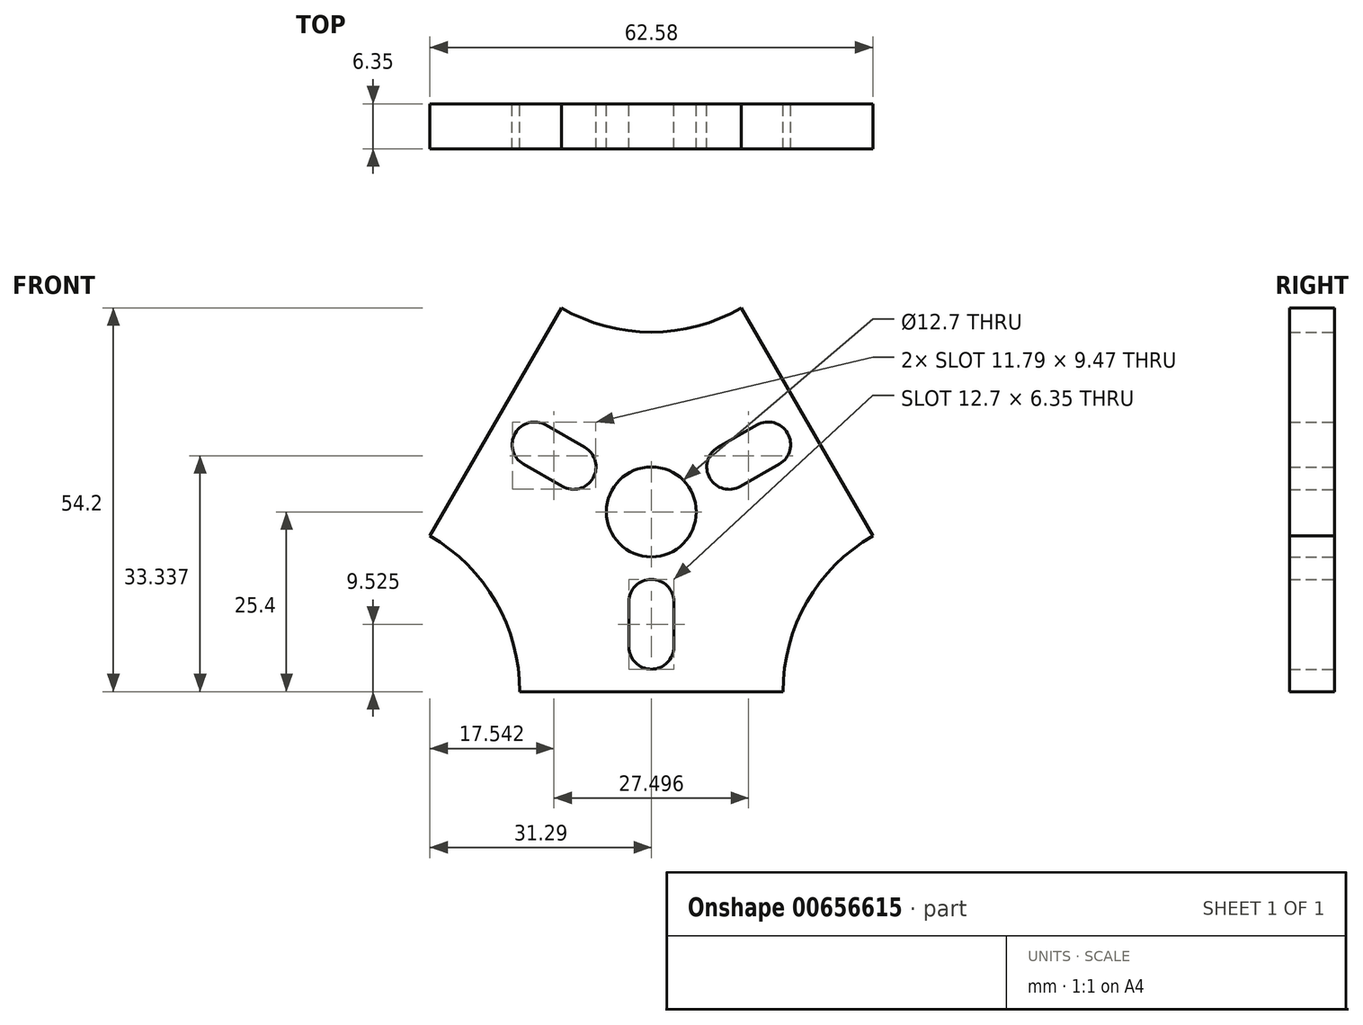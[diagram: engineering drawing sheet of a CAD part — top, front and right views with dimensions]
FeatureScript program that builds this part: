
annotation { "Feature Type Name" : "Feature", "Feature Type Description" : "" }
export const myFeature = defineFeature(function(context is Context, id is Id, definition is map)
    precondition{}
    {
        {
            var Q0;
            Q0=qCreatedBy(makeId("Front.planeOp"),FACE);
            var sketch = newSketch(context, id + "F0", { "sketchPlane" : qUnion([Q0])});
            skCircle(sketch, "E0", {"center": v(0, 0) * mm, "radius": 6.35 * mm});
            skCircle(sketch, "E1.cCircle", {"center": v(0, 0) * mm, "radius": 25.4 * mm, "construction": true});
            skLineSegment(sketch, "E1.0", {"start": v(44, -25.4) * mm, "end": v(-44, -25.4) * mm});
            skLineSegment(sketch, "E1.1", {"start": v(-44, -25.4) * mm, "end": v(0, 50.8) * mm});
            skLineSegment(sketch, "E1.2", {"start": v(0, 50.8) * mm, "end": v(44, -25.4) * mm});
            skPoint(sketch, "E1.0.midPoint", {"position": v(0, -25.4) * mm});
            skCircle(sketch, "E2", {"center": v(0, 0) * mm, "radius": 38.1 * mm});
            skCircle(sketch, "E3", {"center": v(-44, -25.4) * mm, "radius": 25.4 * mm});
            skCircle(sketch, "E4", {"center": v(0, 50.8) * mm, "radius": 25.4 * mm});
            skCircle(sketch, "E5", {"center": v(44, -25.4) * mm, "radius": 25.4 * mm});
            skSolve(sketch);
        }
        {
            var Q0;
            Q0=makeQuery(id+"F0.imprint","IMPRINT",FACE,{"disambiguationData":[TD([[makeQuery(id+"F0.imprint","IMPRINT",EDGE,{"derivedFrom":sQuery(id+"F0.wireOp",EDGE,"E0")}),-1.0]])]});
            extrude(context, id + "F1", {"entities" : qUnion([Q0]), "depth" : 6.35 * mm, "offsetDistance" : 25.4 * mm});
        }
        {
            var Q0;
            Q0=qCreatedBy(makeId("Front.planeOp"),FACE);
            var sketch = newSketch(context, id + "F2", { "sketchPlane" : qUnion([Q0])});
            skPoint(sketch, "E6.center", {"position": v(0, 0) * mm});
            skArc(sketch, "E7", {"start": v(-3.17, -19.05) * mm, "mid": v(0, -22.23) * mm, "end": v(3.17, -19.05) * mm});
            skArc(sketch, "E8", {"start": v(3.18, -12.7) * mm, "mid": v(0, -9.53) * mm, "end": v(-3.18, -12.7) * mm});
            skLineSegment(sketch, "E9", {"start": v(-3.18, -12.7) * mm, "end": v(-3.17, -19.05) * mm});
            skLineSegment(sketch, "E10", {"start": v(3.17, -19.05) * mm, "end": v(3.17, -12.7) * mm});
            skArc(sketch, "E11.1.0", {"start": v(12.59, -3.6) * mm, "mid": v(8.25, -4.76) * mm, "end": v(9.41, -9.1) * mm});
            skLineSegment(sketch, "E11.1.1", {"start": v(18.09, -6.78) * mm, "end": v(12.59, -3.6) * mm});
            skArc(sketch, "E11.1.2", {"start": v(14.91, -12.27) * mm, "mid": v(19.25, -11.11) * mm, "end": v(18.09, -6.78) * mm});
            skLineSegment(sketch, "E11.1.3", {"start": v(9.41, -9.1) * mm, "end": v(14.91, -12.27) * mm});
            skArc(sketch, "E11.2.0", {"start": v(9.41, 9.1) * mm, "mid": v(8.25, 4.76) * mm, "end": v(12.59, 3.6) * mm});
            skLineSegment(sketch, "E11.2.1", {"start": v(14.91, 12.27) * mm, "end": v(9.41, 9.1) * mm});
            skArc(sketch, "E11.2.2", {"start": v(18.09, 6.78) * mm, "mid": v(19.25, 11.11) * mm, "end": v(14.91, 12.27) * mm});
            skLineSegment(sketch, "E11.2.3", {"start": v(12.59, 3.6) * mm, "end": v(18.09, 6.78) * mm});
            skArc(sketch, "E11.3.0", {"start": v(-3.17, 12.7) * mm, "mid": v(0, 9.53) * mm, "end": v(3.18, 12.7) * mm});
            skLineSegment(sketch, "E11.3.1", {"start": v(-3.17, 19.05) * mm, "end": v(-3.17, 12.7) * mm});
            skArc(sketch, "E11.3.2", {"start": v(3.18, 19.05) * mm, "mid": v(0, 22.23) * mm, "end": v(-3.17, 19.05) * mm});
            skLineSegment(sketch, "E11.3.3", {"start": v(3.18, 12.7) * mm, "end": v(3.18, 19.05) * mm});
            skArc(sketch, "E11.4.0", {"start": v(-12.59, 3.6) * mm, "mid": v(-8.25, 4.76) * mm, "end": v(-9.41, 9.1) * mm});
            skLineSegment(sketch, "E11.4.1", {"start": v(-18.09, 6.78) * mm, "end": v(-12.59, 3.6) * mm});
            skArc(sketch, "E11.4.2", {"start": v(-14.91, 12.27) * mm, "mid": v(-19.25, 11.11) * mm, "end": v(-18.09, 6.78) * mm});
            skLineSegment(sketch, "E11.4.3", {"start": v(-9.41, 9.1) * mm, "end": v(-14.91, 12.27) * mm});
            skArc(sketch, "E11.5.0", {"start": v(-9.41, -9.1) * mm, "mid": v(-8.25, -4.76) * mm, "end": v(-12.59, -3.6) * mm});
            skLineSegment(sketch, "E11.5.1", {"start": v(-14.91, -12.27) * mm, "end": v(-9.41, -9.1) * mm});
            skArc(sketch, "E11.5.2", {"start": v(-18.09, -6.78) * mm, "mid": v(-19.25, -11.11) * mm, "end": v(-14.91, -12.27) * mm});
            skLineSegment(sketch, "E11.5.3", {"start": v(-12.59, -3.6) * mm, "end": v(-18.09, -6.78) * mm});
            skSolve(sketch);
        }
        {
            var Q0;
            Q0=makeQuery(id+"F2.imprint","IMPRINT",FACE,{"disambiguationData":[TD([[makeQuery(id+"F2.imprint","IMPRINT",EDGE,{"derivedFrom":sQuery(id+"F2.wireOp",EDGE,"E7")}),1.0]])]});
            var Q1;
            Q1=makeQuery(id+"F2.imprint","IMPRINT",FACE,{"disambiguationData":[TD([[makeQuery(id+"F2.imprint","IMPRINT",EDGE,{"derivedFrom":sQuery(id+"F2.wireOp",EDGE,"E11.4.0")}),1.0]])]});
            var Q2;
            Q2=makeQuery(id+"F2.imprint","IMPRINT",FACE,{"disambiguationData":[TD([[makeQuery(id+"F2.imprint","IMPRINT",EDGE,{"derivedFrom":sQuery(id+"F2.wireOp",EDGE,"E11.2.0")}),1.0]])]});
            extrude(context, id + "F3", {"entities" : qUnion([Q0, Q1, Q2]), "operationType" : NewBodyOperationType.REMOVE, "depth" : 25.4 * mm, "offsetDistance" : 25.4 * mm});
        }
    });
